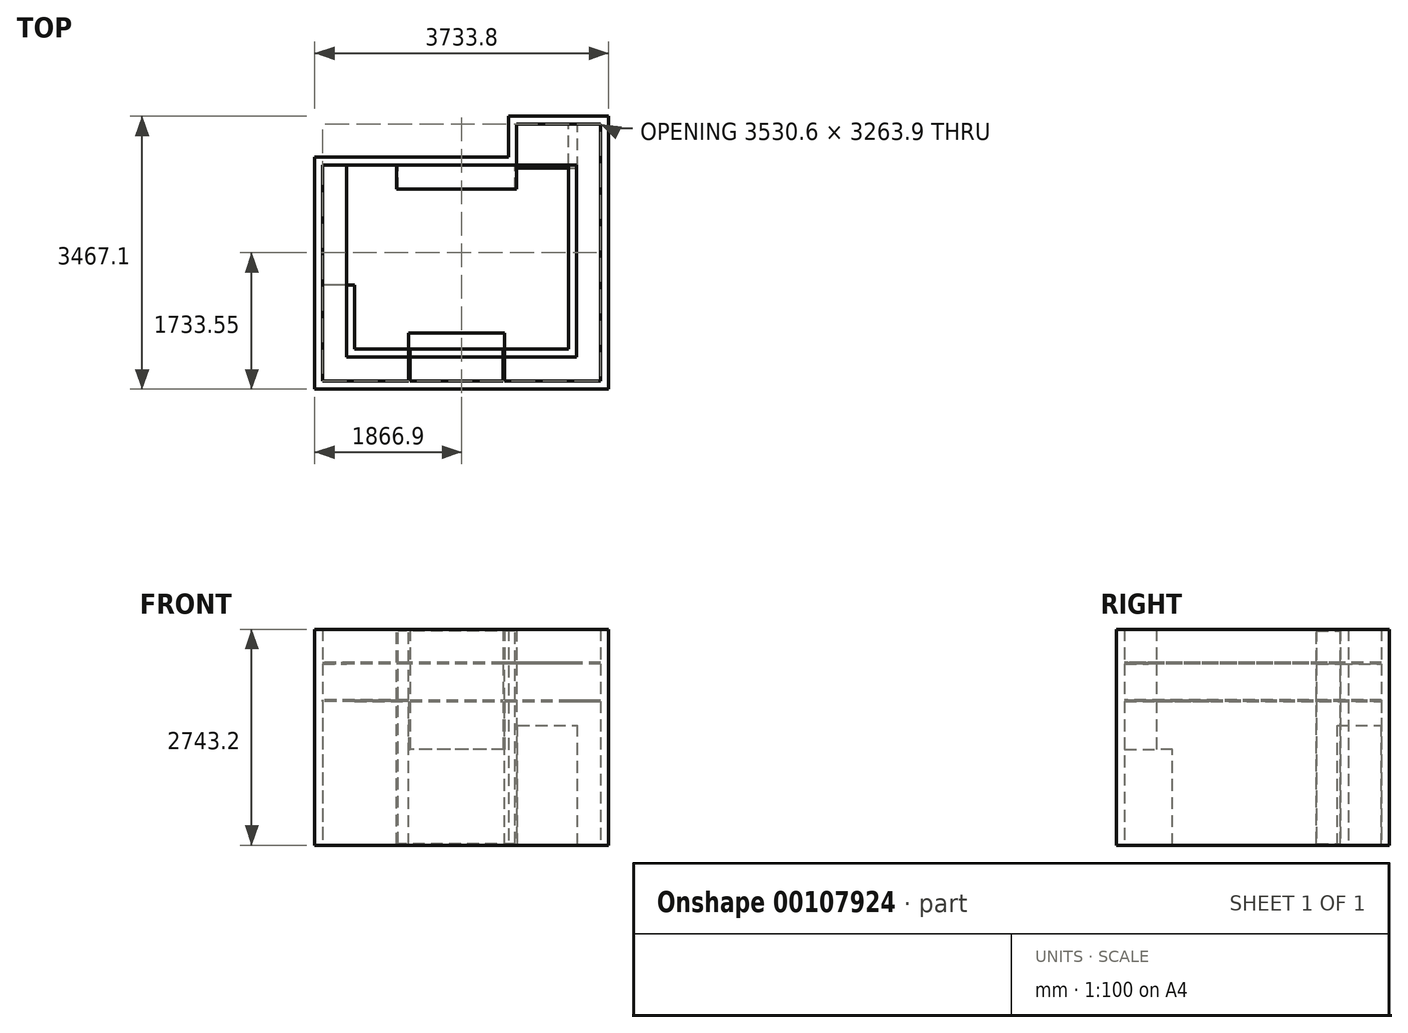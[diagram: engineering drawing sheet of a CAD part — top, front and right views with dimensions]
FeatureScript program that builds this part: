
annotation { "Feature Type Name" : "Feature", "Feature Type Description" : "" }
export const myFeature = defineFeature(function(context is Context, id is Id, definition is map)
    precondition{}
    {
        {
            var Q0;
            Q0=qCreatedBy(makeId("Top.planeOp"),FACE);
            var sketch = newSketch(context, id + "F0", { "sketchPlane" : qUnion([Q0])});
            skLineSegment(sketch, "E0", {"start": v(0, 0) * mm, "end": v(0, 2743.2) * mm});
            skLineSegment(sketch, "E1", {"start": v(0, 2743.2) * mm, "end": v(2463.8, 2743.2) * mm});
            skLineSegment(sketch, "E2", {"start": v(2463.8, 2743.2) * mm, "end": v(2463.8, 3263.9) * mm});
            skLineSegment(sketch, "E3", {"start": v(2463.8, 3263.9) * mm, "end": v(3530.6, 3263.9) * mm});
            skLineSegment(sketch, "E4", {"start": v(3530.6, 3263.9) * mm, "end": v(3530.6, 0) * mm});
            skLineSegment(sketch, "E5", {"start": v(3530.6, 0) * mm, "end": v(0, 0) * mm});
            skLineSegment(sketch, "E6.0", {"start": v(2362.2, 2844.8) * mm, "end": v(2362.2, 3365.5) * mm});
            skLineSegment(sketch, "E6.1", {"start": v(3632.2, 3365.5) * mm, "end": v(3632.2, -101.6) * mm});
            skLineSegment(sketch, "E6.2", {"start": v(3632.2, -101.6) * mm, "end": v(-101.6, -101.6) * mm});
            skLineSegment(sketch, "E6.3", {"start": v(2362.2, 3365.5) * mm, "end": v(3632.2, 3365.5) * mm});
            skLineSegment(sketch, "E6.4", {"start": v(-101.6, -101.6) * mm, "end": v(-101.6, 2844.8) * mm});
            skLineSegment(sketch, "E6.5", {"start": v(-101.6, 2844.8) * mm, "end": v(2362.2, 2844.8) * mm});
            skSolve(sketch);
        }
        {
            var Q0;
            Q0=makeQuery(id+"F0.imprint","IMPRINT",FACE,{"disambiguationData":[TD([[makeQuery(id+"F0.imprint","IMPRINT",EDGE,{"derivedFrom":sQuery(id+"F0.wireOp",EDGE,"E0")}),1.0]])]});
            extrude(context, id + "F1", {"entities" : qUnion([Q0]), "depth" : 2743.2 * mm});
        }
        {
            var Q0;
            Q0=makeQuery(id+"F1.opExtrude","SWEPT_FACE",FACE,{"disambiguationData":[OSD([sQuery(id+"F0.wireOp",EDGE,"E3")])]});
            var sketch = newSketch(context, id + "F2", { "sketchPlane" : qUnion([Q0])});
            skLineSegment(sketch, "E7.bottom", {"start": v(2476.5, 0) * mm, "end": v(3238.5, 0) * mm});
            skLineSegment(sketch, "E7.top", {"start": v(2476.5, 1524) * mm, "end": v(3238.5, 1524) * mm});
            skLineSegment(sketch, "E7.left", {"start": v(2476.5, 0) * mm, "end": v(2476.5, 1524) * mm});
            skLineSegment(sketch, "E7.right", {"start": v(3238.5, 0) * mm, "end": v(3238.5, 1524) * mm});
            skSolve(sketch);
        }
        {
            var Q0;
            Q0 = qSketchRegion(id + "F2", true);
            extrude(context, id + "F3", {"entities" : qUnion([Q0]), "operationType" : NewBodyOperationType.ADD, "depth" : 558.8 * mm});
        }
        {
            var Q0;
            Q0=makeQuery(id+"F1.opExtrude","SWEPT_FACE",FACE,{"disambiguationData":[OSD([sQuery(id+"F0.wireOp",EDGE,"E1")])]});
            var sketch = newSketch(context, id + "F4", { "sketchPlane" : qUnion([Q0])});
            skLineSegment(sketch, "E8.bottom", {"start": v(2463.8, 0) * mm, "end": v(939.8, 0) * mm});
            skLineSegment(sketch, "E8.top", {"start": v(2463.8, 2743.2) * mm, "end": v(939.8, 2743.2) * mm});
            skLineSegment(sketch, "E8.left", {"start": v(2463.8, 0) * mm, "end": v(2463.8, 2743.2) * mm});
            skLineSegment(sketch, "E8.right", {"start": v(939.8, 0) * mm, "end": v(939.8, 2743.2) * mm});
            skLineSegment(sketch, "E9.0", {"start": v(2444.75, 19.05) * mm, "end": v(958.85, 19.05) * mm});
            skLineSegment(sketch, "E9.1", {"start": v(2444.75, 19.05) * mm, "end": v(2444.75, 2724.15) * mm});
            skLineSegment(sketch, "E9.2", {"start": v(2444.75, 2724.15) * mm, "end": v(958.85, 2724.15) * mm});
            skLineSegment(sketch, "E9.3", {"start": v(958.85, 19.05) * mm, "end": v(958.85, 2724.15) * mm});
            skLineSegment(sketch, "E10.0", {"start": v(-95.25, 6.35) * mm, "end": v(3625.85, 6.35) * mm});
            skLineSegment(sketch, "E10.1", {"start": v(-95.25, 2736.85) * mm, "end": v(-95.25, 6.35) * mm});
            skLineSegment(sketch, "E10.2", {"start": v(3625.85, 2736.85) * mm, "end": v(-95.25, 2736.85) * mm});
            skLineSegment(sketch, "E10.3", {"start": v(3625.85, 6.35) * mm, "end": v(3625.85, 2736.85) * mm});
            skSolve(sketch);
        }
        {
            var Q0;
            Q0=makeQuery(id+"F4.imprint","IMPRINT",FACE,{"disambiguationData":[TD([[makeQuery(id+"F4.imprint","IMPRINT",EDGE,{"derivedFrom":sQuery(id+"F4.wireOp",EDGE,"E9.0")}),1.0]])]});
            extrude(context, id + "F5", {"entities" : qUnion([Q0]), "depth" : 304.8 * mm});
        }
        {
            var Q0;
            Q0=makeQuery(id+"F1.opExtrude","SWEPT_FACE",FACE,{"disambiguationData":[OSD([sQuery(id+"F0.wireOp",EDGE,"E0")])]});
            var sketch = newSketch(context, id + "F6", { "sketchPlane" : qUnion([Q0])});
            skLineSegment(sketch, "E11.bottom", {"start": v(0, 1828.8) * mm, "end": v(1219.2, 1828.8) * mm});
            skLineSegment(sketch, "E11.top", {"start": v(0, 1847.85) * mm, "end": v(1219.2, 1847.85) * mm});
            skLineSegment(sketch, "E11.left", {"start": v(0, 1828.8) * mm, "end": v(0, 1847.85) * mm});
            skLineSegment(sketch, "E11.right", {"start": v(1219.2, 1828.8) * mm, "end": v(1219.2, 1847.85) * mm});
            skSolve(sketch);
        }
        {
            var Q0;
            Q0 = qSketchRegion(id + "F6", true);
            extrude(context, id + "F7", {"entities" : qUnion([Q0]), "operationType" : NewBodyOperationType.ADD, "depth" : 406.4 * mm});
        }
        {
            var Q0;
            Q0=makeQuery(id+"F1.opExtrude","SWEPT_FACE",FACE,{"disambiguationData":[OSD([sQuery(id+"F0.wireOp",EDGE,"E5")])]});
            var sketch = newSketch(context, id + "F8", { "sketchPlane" : qUnion([Q0])});
            skLineSegment(sketch, "E12.bottom", {"start": v(-2311.4, 0) * mm, "end": v(-1092.2, 0) * mm});
            skLineSegment(sketch, "E12.top", {"start": v(-2311.4, 1219.2) * mm, "end": v(-1092.2, 1219.2) * mm});
            skLineSegment(sketch, "E12.left", {"start": v(-2311.4, 0) * mm, "end": v(-2311.4, 1219.2) * mm});
            skLineSegment(sketch, "E12.right", {"start": v(-1092.2, 0) * mm, "end": v(-1092.2, 1219.2) * mm});
            skSolve(sketch);
        }
        {
            var Q0;
            Q0 = qSketchRegion(id + "F8", true);
            extrude(context, id + "F9", {"entities" : qUnion([Q0]), "operationType" : NewBodyOperationType.ADD, "depth" : 609.6 * mm});
        }
        {
            var Q0;
            Q0=makeQuery(id+"F9.opExtrude","SWEPT_FACE",FACE,{"disambiguationData":[OSD([sQuery(id+"F8.wireOp",EDGE,"E12.top")])]});
            var sketch = newSketch(context, id + "F10", { "sketchPlane" : qUnion([Q0])});
            skLineSegment(sketch, "E13.bottom", {"start": v(2311.4, 0) * mm, "end": v(2292.35, 0) * mm});
            skLineSegment(sketch, "E13.top", {"start": v(2311.4, 406.4) * mm, "end": v(2292.35, 406.4) * mm});
            skLineSegment(sketch, "E13.left", {"start": v(2311.4, 0) * mm, "end": v(2311.4, 406.4) * mm});
            skLineSegment(sketch, "E13.right", {"start": v(2292.35, 0) * mm, "end": v(2292.35, 406.4) * mm});
            skLineSegment(sketch, "E14.bottom", {"start": v(1092.2, 0) * mm, "end": v(1111.25, 0) * mm});
            skLineSegment(sketch, "E14.top", {"start": v(1092.2, 406.4) * mm, "end": v(1111.25, 406.4) * mm});
            skLineSegment(sketch, "E14.left", {"start": v(1092.2, 0) * mm, "end": v(1092.2, 406.4) * mm});
            skLineSegment(sketch, "E14.right", {"start": v(1111.25, 0) * mm, "end": v(1111.25, 406.4) * mm});
            skSolve(sketch);
        }
        {
            var Q0;
            Q0 = qSketchRegion(id + "F10", true);
            extrude(context, id + "F11", {"entities" : qUnion([Q0]), "operationType" : NewBodyOperationType.ADD, "depth" : 1524 * mm});
        }
        {
            var Q0;
            {var subQ1=sQuery(id+"F0.wireOp",EDGE,"E0");var subQ8=sQuery(id+"F0.wireOp",EDGE,"E5");Q0=makeQuery(id+"F11.boolean.opBoolean","SPLIT",FACE,{"disambiguationData":[TD([makeQuery(id+"F1.opExtrude","SWEPT_FACE",FACE,{"disambiguationData":[OSD([subQ1])]})])],"derivedFrom":makeQuery(id+"F1.opExtrude","SWEPT_FACE",FACE,{"disambiguationData":[OSD([subQ8])]})});}
            var sketch = newSketch(context, id + "F12", { "sketchPlane" : qUnion([Q0])});
            skLineSegment(sketch, "E15.bottom", {"start": v(-406.4, 1847.85) * mm, "end": v(-3530.6, 1847.85) * mm});
            skLineSegment(sketch, "E15.top", {"start": v(-406.4, 1828.8) * mm, "end": v(-3530.6, 1828.8) * mm});
            skLineSegment(sketch, "E15.left", {"start": v(-406.4, 1847.85) * mm, "end": v(-406.4, 1828.8) * mm});
            skLineSegment(sketch, "E15.right", {"start": v(-3530.6, 1847.85) * mm, "end": v(-3530.6, 1828.8) * mm});
            skSolve(sketch);
        }
        {
            var Q0;
            Q0 = qSketchRegion(id + "F12", true);
            extrude(context, id + "F13", {"entities" : qUnion([Q0]), "operationType" : NewBodyOperationType.ADD, "depth" : 406.4 * mm});
        }
        {
            var Q0;
            Q0=makeQuery(id+"F1.opExtrude","SWEPT_FACE",FACE,{"disambiguationData":[OSD([sQuery(id+"F0.wireOp",EDGE,"E4")])]});
            var sketch = newSketch(context, id + "F14", { "sketchPlane" : qUnion([Q0])});
            skLineSegment(sketch, "E16.bottom", {"start": v(-406.4, 1847.85) * mm, "end": v(-3263.9, 1847.85) * mm});
            skLineSegment(sketch, "E16.top", {"start": v(-406.4, 1828.8) * mm, "end": v(-3263.9, 1828.8) * mm});
            skLineSegment(sketch, "E16.left", {"start": v(-406.4, 1847.85) * mm, "end": v(-406.4, 1828.8) * mm});
            skLineSegment(sketch, "E16.right", {"start": v(-3263.9, 1847.85) * mm, "end": v(-3263.9, 1828.8) * mm});
            skSolve(sketch);
        }
        {
            var Q0;
            Q0 = qSketchRegion(id + "F14", true);
            extrude(context, id + "F15", {"entities" : qUnion([Q0]), "operationType" : NewBodyOperationType.ADD, "depth" : 406.4 * mm});
        }
        {
            var Q0;
            {var subQ5=sQuery(id+"F0.wireOp",EDGE,"E5");Q0=makeQuery(id+"F13.boolean.opBoolean","SPLIT",FACE,{"disambiguationData":[TD([makeQuery(id+"F13.opExtrude","SWEPT_FACE",FACE,{"disambiguationData":[OSD([sQuery(id+"F12.wireOp",EDGE,"E15.bottom")])]})])],"derivedFrom":makeQuery(id+"F11.boolean.opBoolean","SPLIT",FACE,{"disambiguationData":[TD([makeQuery(id+"F9.opExtrude","SWEPT_FACE",FACE,{"disambiguationData":[OSD([sQuery(id+"F8.wireOp",EDGE,"E12.top")])]})])],"derivedFrom":makeQuery(id+"F1.opExtrude","SWEPT_FACE",FACE,{"disambiguationData":[OSD([subQ5])]})})});}
            var sketch = newSketch(context, id + "F16", { "sketchPlane" : qUnion([Q0])});
            skLineSegment(sketch, "E17.bottom", {"start": v(-3530.6, 2324.1) * mm, "end": v(0, 2324.1) * mm});
            skLineSegment(sketch, "E17.top", {"start": v(-3530.6, 2305.05) * mm, "end": v(0, 2305.05) * mm});
            skLineSegment(sketch, "E17.left", {"start": v(-3530.6, 2324.1) * mm, "end": v(-3530.6, 2305.05) * mm});
            skLineSegment(sketch, "E17.right", {"start": v(0, 2324.1) * mm, "end": v(0, 2305.05) * mm});
            skSolve(sketch);
        }
        {
            var Q0;
            Q0 = qSketchRegion(id + "F16", true);
            var Q1;
            Q1=makeQuery(id+"F1.opExtrude","SWEPT_FACE",FACE,{"disambiguationData":[OSD([sQuery(id+"F0.wireOp",EDGE,"E3")])]});
            extrude(context, id + "F17", {"entities" : qUnion([Q0]), "operationType" : NewBodyOperationType.ADD, "endBound" : BoundingType.UP_TO_SURFACE, "endBoundEntityFace" : qUnion([Q1]), "depth" : 2235.2 * mm});
        }
        {
            var Q0;
            Q0=makeQuery(id+"F17.opExtrude","SWEPT_FACE",FACE,{"disambiguationData":[OSD([sQuery(id+"F16.wireOp",EDGE,"E17.bottom")])]});
            var sketch = newSketch(context, id + "F18", { "sketchPlane" : qUnion([Q0])});
            skLineSegment(sketch, "E18.bottom", {"start": v(3225.8, 2743.2) * mm, "end": v(304.8, 2743.2) * mm});
            skLineSegment(sketch, "E18.top", {"start": v(3225.8, 304.8) * mm, "end": v(304.8, 304.8) * mm});
            skLineSegment(sketch, "E18.left", {"start": v(3225.8, 2743.2) * mm, "end": v(3225.8, 304.8) * mm});
            skLineSegment(sketch, "E18.right", {"start": v(304.8, 2743.2) * mm, "end": v(304.8, 304.8) * mm});
            skSolve(sketch);
        }
        {
            var Q0;
            Q0 = qSketchRegion(id + "F18", true);
            extrude(context, id + "F19", {"entities" : qUnion([Q0]), "operationType" : NewBodyOperationType.REMOVE, "oppositeDirection" : true, "depth" : 19.05 * mm});
        }
        {
            var Q0;
            Q0=makeQuery(id+"F17.boolean.opBoolean","SPLIT",FACE,{"disambiguationData":[TD([makeQuery(id+"F1.opExtrude","SWEPT_FACE",FACE,{"disambiguationData":[OSD([sQuery(id+"F0.wireOp",EDGE,"E6.0")])]})])],"derivedFrom":makeQuery(id+"F17.opExtrude","SWEPT_FACE",FACE,{"disambiguationData":[OSD([sQuery(id+"F16.wireOp",EDGE,"E17.bottom")])]})});
            var sketch = newSketch(context, id + "F20", { "sketchPlane" : qUnion([Q0])});
            skLineSegment(sketch, "E19.0", {"start": v(0, 2844.8) * mm, "end": v(2362.2, 2844.8) * mm});
            skLineSegment(sketch, "E19.1", {"start": v(0, 3263.9) * mm, "end": v(0, 2844.8) * mm});
            skLineSegment(sketch, "E19.2", {"start": v(2362.2, 3263.9) * mm, "end": v(0, 3263.9) * mm});
            skLineSegment(sketch, "E19.3", {"start": v(2362.2, 2844.8) * mm, "end": v(2362.2, 3263.9) * mm});
            skSolve(sketch);
        }
        {
            var Q0;
            Q0 = qSketchRegion(id + "F20", true);
            extrude(context, id + "F21", {"entities" : qUnion([Q0]), "operationType" : NewBodyOperationType.REMOVE, "endBound" : BoundingType.THROUGH_ALL, "oppositeDirection" : true, "depth" : 25.4 * mm});
        }
    });
